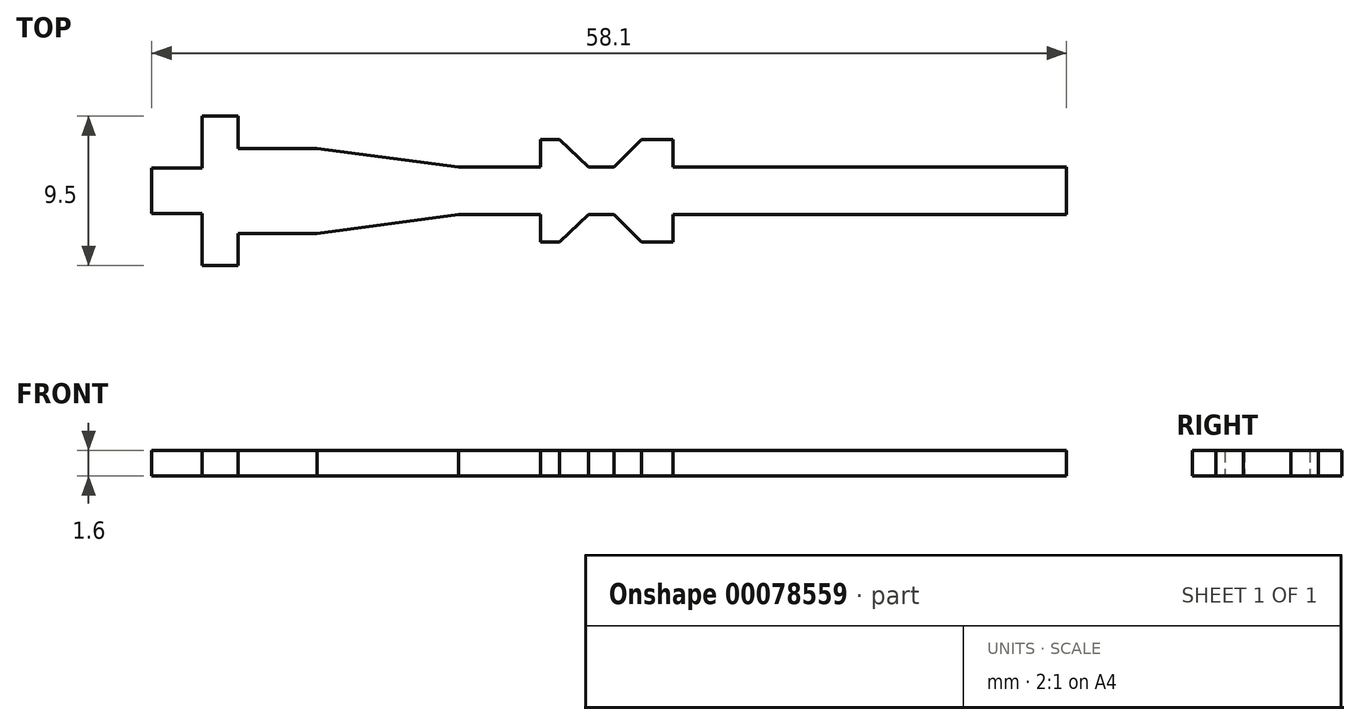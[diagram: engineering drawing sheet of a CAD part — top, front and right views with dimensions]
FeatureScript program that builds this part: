
annotation { "Feature Type Name" : "Feature", "Feature Type Description" : "" }
export const myFeature = defineFeature(function(context is Context, id is Id, definition is map)
    precondition{}
    {
        {
            var Q0;
            Q0=qCreatedBy(makeId("Top.planeOp"),FACE);
            var sketch = newSketch(context, id + "F0", { "sketchPlane" : qUnion([Q0])});
            skLineSegment(sketch, "E0", {"start": v(0, 0) * mm, "end": v(-60.33, 0) * mm, "construction": true});
            skLineSegment(sketch, "E1", {"start": v(0, 0) * mm, "end": v(0, 1.5) * mm});
            skLineSegment(sketch, "E2", {"start": v(0, 1.5) * mm, "end": v(-25, 1.5) * mm});
            skLineSegment(sketch, "E3", {"start": v(-25, 1.5) * mm, "end": v(-25, 3.25) * mm});
            skLineSegment(sketch, "E4", {"start": v(-25, 3.25) * mm, "end": v(-27, 3.25) * mm});
            skLineSegment(sketch, "E5", {"start": v(-27, 3.25) * mm, "end": v(-28.75, 1.5) * mm});
            skLineSegment(sketch, "E6", {"start": v(-28.75, 1.5) * mm, "end": v(-30.35, 1.5) * mm});
            skLineSegment(sketch, "E7", {"start": v(-30.35, 1.5) * mm, "end": v(-32.2, 3.25) * mm});
            skLineSegment(sketch, "E8", {"start": v(-32.2, 3.25) * mm, "end": v(-33.4, 3.25) * mm});
            skLineSegment(sketch, "E9", {"start": v(-33.4, 3.25) * mm, "end": v(-33.4, 1.5) * mm});
            skLineSegment(sketch, "E10", {"start": v(-33.4, 1.5) * mm, "end": v(-38.6, 1.5) * mm});
            skLineSegment(sketch, "E11", {"start": v(-38.6, 1.5) * mm, "end": v(-47.6, 2.7) * mm});
            skLineSegment(sketch, "E12", {"start": v(-47.6, 2.7) * mm, "end": v(-52.6, 2.7) * mm});
            skLineSegment(sketch, "E13", {"start": v(-52.6, 2.7) * mm, "end": v(-52.6, 4.75) * mm});
            skLineSegment(sketch, "E14", {"start": v(-52.6, 4.75) * mm, "end": v(-54.9, 4.75) * mm});
            skLineSegment(sketch, "E15", {"start": v(-54.9, 4.75) * mm, "end": v(-54.9, 1.45) * mm});
            skLineSegment(sketch, "E16", {"start": v(-54.9, 1.45) * mm, "end": v(-58.1, 1.45) * mm});
            skLineSegment(sketch, "E17", {"start": v(-58.1, 1.45) * mm, "end": v(-58.1, 0) * mm});
            skLineSegment(sketch, "E18.MirrorCS", {"start": v(-32.2, -3.25) * mm, "end": v(-33.4, -3.25) * mm});
            skLineSegment(sketch, "E19.MirrorCS", {"start": v(-27, -3.25) * mm, "end": v(-28.75, -1.5) * mm});
            skLineSegment(sketch, "E20.MirrorCS", {"start": v(-47.6, -2.7) * mm, "end": v(-52.6, -2.7) * mm});
            skLineSegment(sketch, "E21.MirrorCS", {"start": v(-52.6, -2.7) * mm, "end": v(-52.6, -4.75) * mm});
            skLineSegment(sketch, "E22.MirrorCS", {"start": v(0, -1.5) * mm, "end": v(-25, -1.5) * mm});
            skLineSegment(sketch, "E23.MirrorCS", {"start": v(-58.1, -1.45) * mm, "end": v(-58.1, 0) * mm});
            skLineSegment(sketch, "E24.MirrorCS", {"start": v(-25, -3.25) * mm, "end": v(-27, -3.25) * mm});
            skLineSegment(sketch, "E25.MirrorCS", {"start": v(-25, -1.5) * mm, "end": v(-25, -3.25) * mm});
            skLineSegment(sketch, "E26.MirrorCS", {"start": v(-54.9, -4.75) * mm, "end": v(-54.9, -1.45) * mm});
            skLineSegment(sketch, "E27.MirrorCS", {"start": v(-28.75, -1.5) * mm, "end": v(-30.35, -1.5) * mm});
            skLineSegment(sketch, "E28.MirrorCS", {"start": v(-54.9, -1.45) * mm, "end": v(-58.1, -1.45) * mm});
            skLineSegment(sketch, "E29.MirrorCS", {"start": v(0, 0) * mm, "end": v(0, -1.5) * mm});
            skLineSegment(sketch, "E30.MirrorCS", {"start": v(-33.4, -3.25) * mm, "end": v(-33.4, -1.5) * mm});
            skLineSegment(sketch, "E31.MirrorCS", {"start": v(-52.6, -4.75) * mm, "end": v(-54.9, -4.75) * mm});
            skLineSegment(sketch, "E32.MirrorCS", {"start": v(-33.4, -1.5) * mm, "end": v(-38.6, -1.5) * mm});
            skLineSegment(sketch, "E33.MirrorCS", {"start": v(-38.6, -1.5) * mm, "end": v(-47.6, -2.7) * mm});
            skLineSegment(sketch, "E34.MirrorCS", {"start": v(-30.35, -1.5) * mm, "end": v(-32.2, -3.25) * mm});
            skSolve(sketch);
        }
        {
            var Q0;
            Q0 = qSketchRegion(id + "F0", true);
            extrude(context, id + "F1", {"entities" : qUnion([Q0]), "depth" : 1.6 * mm});
        }
    });
